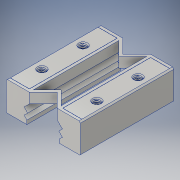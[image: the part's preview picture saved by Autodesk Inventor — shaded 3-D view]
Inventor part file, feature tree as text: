
AUTODESK INVENTOR PART (.ipt)
format: ipt  version: 2016 (Build 200138000, 138)  size: 935,936 bytes
history: native  units: in
note: dims shown in document units (in); Inventor stores cm internally (conversion verified against a paired STEP export)
features: mirror x1
ambient origin geometry x8: Origin, YZ Plane, XZ Plane, XY Plane, X Axis, Y Axis, Z Axis, Center Point
bodies: Solid1 (feature_tree)
feature tree (1):
  mirror  "Mirror1"
